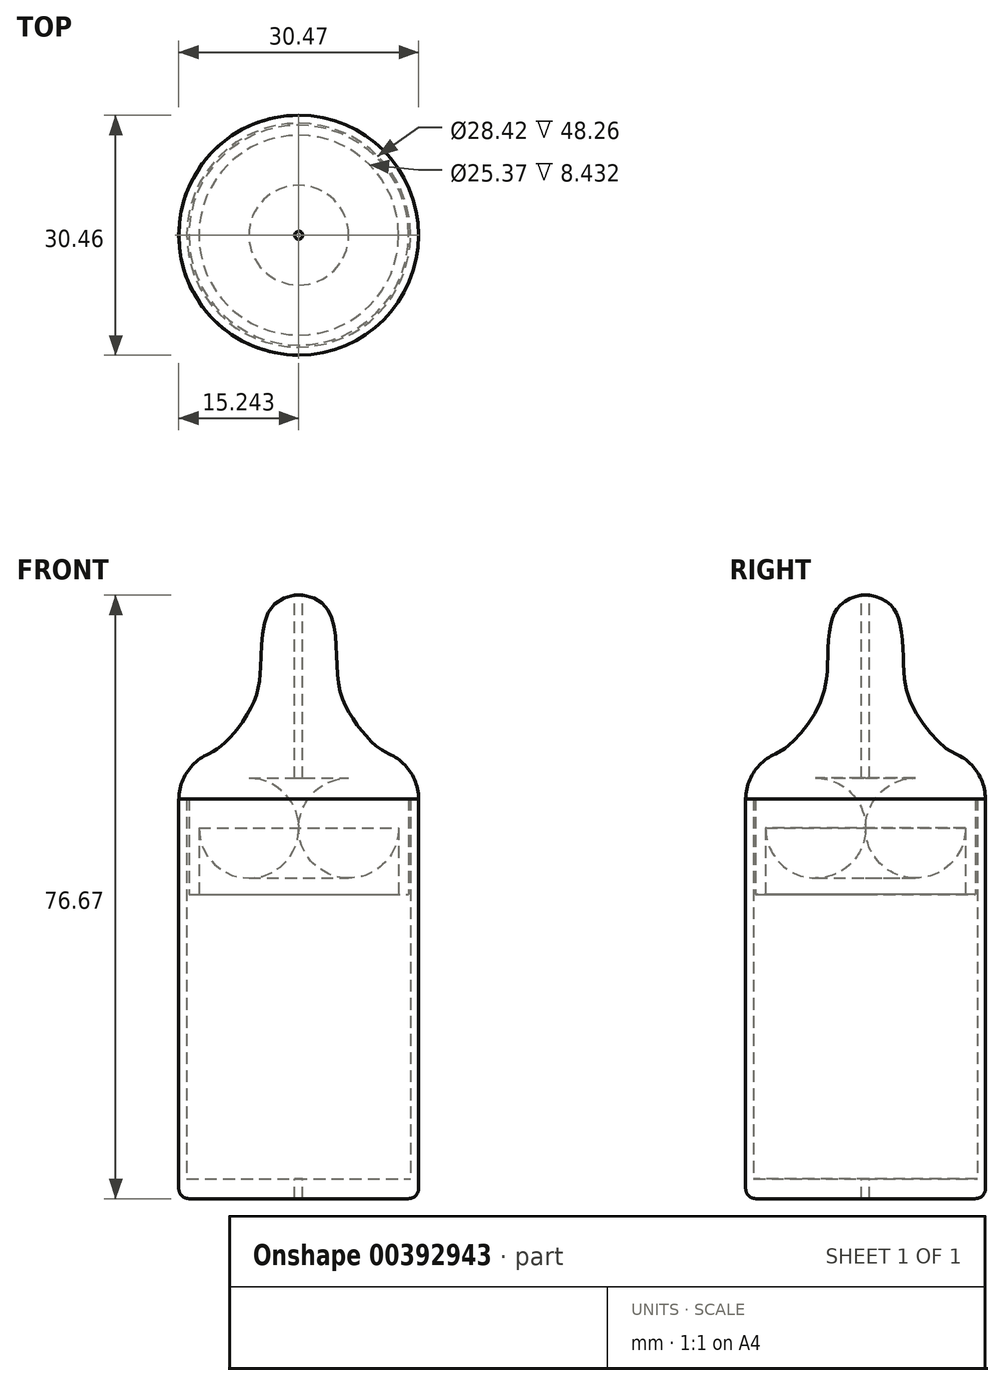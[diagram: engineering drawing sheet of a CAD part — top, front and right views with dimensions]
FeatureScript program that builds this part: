
annotation { "Feature Type Name" : "Feature", "Feature Type Description" : "" }
export const myFeature = defineFeature(function(context is Context, id is Id, definition is map)
    precondition{}
    {
        {
            var Q0;
            Q0=qCreatedBy(makeId("Front.planeOp"),FACE);
            var sketch = newSketch(context, id + "F0", { "sketchPlane" : qUnion([Q0])});
            skLineSegment(sketch, "E0", {"start": v(0.01, 14.78) * mm, "end": v(0.01, 38.09) * mm});
            skLineSegment(sketch, "E1", {"start": v(12.7, 0) * mm, "end": v(13.97, 0) * mm});
            skFitSpline(sketch, "E2", {"points": [v(0.01, 38.09) * mm, v(4.52, 33.84) * mm, v(5.04, 26.88) * mm, v(6.71, 22.6) * mm, v(9.3, 19.39) * mm, v(15.54, 16.85) * mm], "startDerivative": vector(46.27, -4.35) * mm, "endDerivative": vector(52.64, -7.46) * mm});
            skLineSegment(sketch, "E3", {"start": v(0.01, 14.78) * mm, "end": v(6.35, 14.78) * mm});
            skLineSegment(sketch, "E4", {"start": v(12.7, 8.43) * mm, "end": v(12.7, 0) * mm});
            skPoint(sketch, "E5.visualSharp", {"position": v(12.7, 14.78) * mm});
            skArc(sketch, "E5.filletArc", {"start": v(12.7, 8.43) * mm, "mid": v(10.84, 12.92) * mm, "end": v(6.35, 14.78) * mm});
            skArc(sketch, "E6.filletArc", {"start": v(15.24, 12.16) * mm, "mid": v(14.19, 15.57) * mm, "end": v(11.46, 17.87) * mm});
            skLineSegment(sketch, "E7", {"start": v(15.24, 12.16) * mm, "end": v(13.97, 12.16) * mm});
            skLineSegment(sketch, "E8", {"start": v(13.97, 12.16) * mm, "end": v(13.97, 0) * mm});
            skSolve(sketch);
        }
        {
            var Q0;
            Q0=makeQuery(id+"F0.imprint","IMPRINT",FACE,{"disambiguationData":[TD([[makeQuery(id+"F0.imprint","IMPRINT",EDGE,{"derivedFrom":sQuery(id+"F0.wireOp",EDGE,"E0")}),-1.0]])]});
            var Q1;
            Q1=sQuery(id+"F0.wireOp",EDGE,"E0");
            revolve(context, id + "F1", {"entities" : qUnion([Q0]), "axis" : qUnion([Q1]), "revolveType" : RevolveType.FULL});
        }
        {
            var Q0;
            Q0=qCreatedBy(makeId("Right.planeOp"),FACE);
            var sketch = newSketch(context, id + "F2", { "sketchPlane" : qUnion([Q0])});
            skLineSegment(sketch, "E9", {"start": v(0, -38.64) * mm, "end": v(0, -36.1) * mm});
            skLineSegment(sketch, "E10", {"start": v(-15.23, 12.16) * mm, "end": v(-15.23, -38.64) * mm});
            skLineSegment(sketch, "E11", {"start": v(0, -38.64) * mm, "end": v(-15.23, -38.64) * mm});
            skPoint(sketch, "E12.orphan", {"position": v(0, -9.87) * mm});
            skPoint(sketch, "E13.orphan", {"position": v(-15.23, 12.16) * mm});
            skLineSegment(sketch, "E14", {"start": v(-14.21, 12.16) * mm, "end": v(-14.21, -36.1) * mm});
            skLineSegment(sketch, "E15", {"start": v(-14.21, -36.1) * mm, "end": v(0, -36.1) * mm});
            skLineSegment(sketch, "E16.trimOffspring", {"start": v(-14.21, 12.16) * mm, "end": v(-15.23, 12.16) * mm});
            skPoint(sketch, "E17.0.start.orphan", {"position": v(15.23, 12.16) * mm});
            skSolve(sketch);
        }
        {
            var Q0;
            Q0 = qSketchRegion(id + "F2", true);
            var Q1;
            Q1=sQuery(id+"F2.wireOp",EDGE,"E9");
            revolve(context, id + "F3", {"entities" : qUnion([Q0]), "axis" : qUnion([Q1]), "revolveType" : RevolveType.FULL});
        }
        {
            var Q0;
            Q0=makeQuery(id+"F3.opRevolve","SWEPT_EDGE",EDGE,{"disambiguationData":[OSD([sQuery(id+"F2.wireOp",EDGE,"E10"),sQuery(id+"F2.wireOp",EDGE,"E11")])]});
            fillet(context, id + "F4", {"entities" : qUnion([Q0]), "radius" : 1.27 * mm, "tangentPropagation" : true, "allowEdgeOverflow" : false});
        }
        {
            var Q0;
            Q0=qCreatedBy(makeId("Top.planeOp"),FACE);
            cPlane(context, id + "F5", {"entities" : qUnion([Q0]), "cplaneType" : CPlaneType.OFFSET, "offset" : 38.1 * mm, "width" : 152.4 * mm, "height" : 152.4 * mm});
        }
        {
            var Q0;
            Q0=qCreatedBy(id+"F5.planeOp",FACE);
            var sketch = newSketch(context, id + "F6", { "sketchPlane" : qUnion([Q0])});
            skCircle(sketch, "E18", {"center": v(0, 0) * mm, "radius": 0.5 * mm});
            skSolve(sketch);
        }
        {
            var Q0;
            Q0 = qSketchRegion(id + "F6", true);
            extrude(context, id + "F7", {"entities" : qUnion([Q0]), "operationType" : NewBodyOperationType.REMOVE, "oppositeDirection" : true, "depth" : 2540 * mm, "offsetDistance" : 25.4 * mm});
        }
    });
